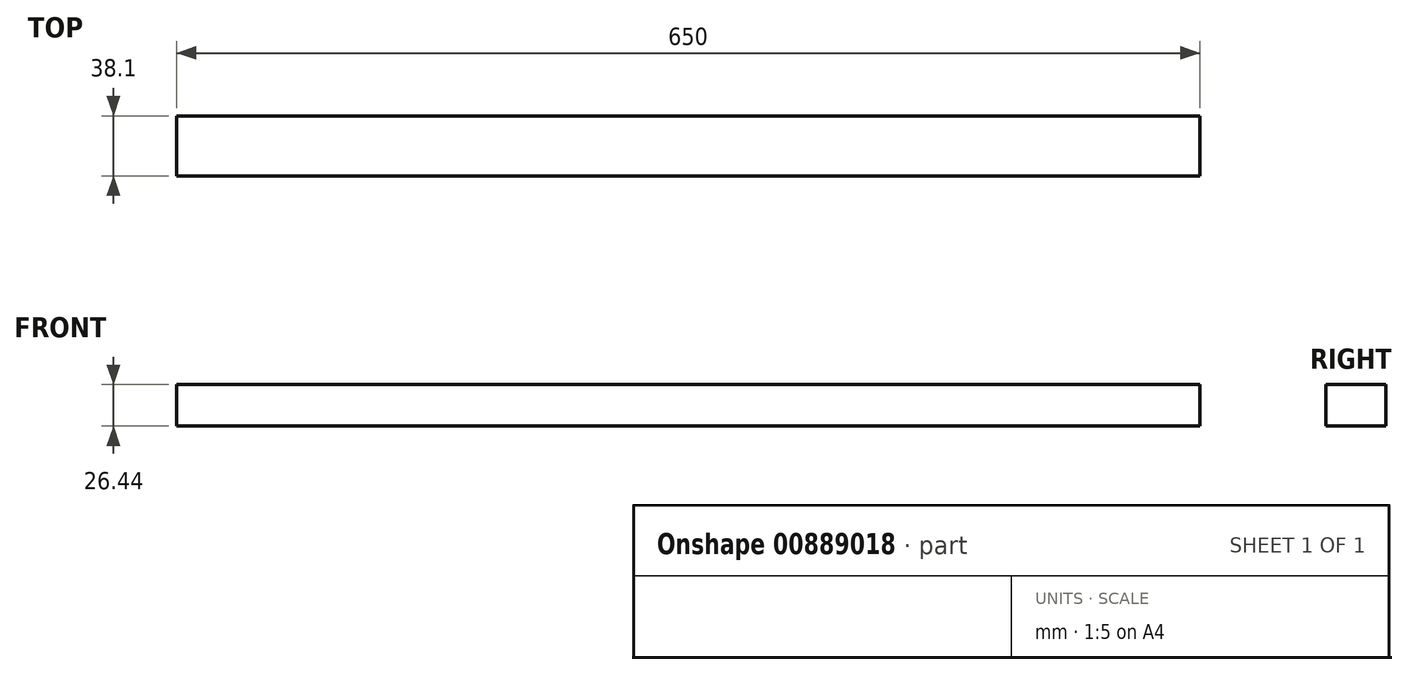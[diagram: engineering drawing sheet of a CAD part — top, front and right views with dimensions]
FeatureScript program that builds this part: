
annotation { "Feature Type Name" : "Feature", "Feature Type Description" : "" }
export const myFeature = defineFeature(function(context is Context, id is Id, definition is map)
    precondition{}
    {
        {
            var Q0;
            Q0=qCreatedBy(makeId("Right.planeOp"),FACE);
            var sketch = newSketch(context, id + "F0", { "sketchPlane" : qUnion([Q0])});
            skLineSegment(sketch, "E0.bottom", {"start": v(-19.05, 13.22) * mm, "end": v(19.05, 13.22) * mm});
            skLineSegment(sketch, "E0.top", {"start": v(-19.05, -13.22) * mm, "end": v(19.05, -13.22) * mm});
            skLineSegment(sketch, "E0.left", {"start": v(-19.05, 13.22) * mm, "end": v(-19.05, -13.22) * mm});
            skLineSegment(sketch, "E0.right", {"start": v(19.05, 13.22) * mm, "end": v(19.05, -13.22) * mm});
            skPoint(sketch, "E0.middle", {"position": v(0, 0) * mm});
            skSolve(sketch);
        }
        {
            var Q0;
            Q0 = qSketchRegion(id + "F0", true);
            extrude(context, id + "F1", {"entities" : qUnion([Q0]), "depth" : 650 * mm, "offsetDistance" : 25 * mm});
        }
    });
